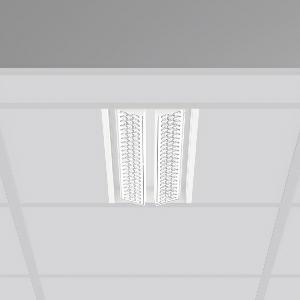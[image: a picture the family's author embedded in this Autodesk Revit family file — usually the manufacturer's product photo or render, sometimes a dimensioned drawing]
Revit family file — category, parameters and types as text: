
# Revit family: tx-move_901736_002_3_d08b
name_source: partatom
category: Lighting Fixtures
units: mm (PartAtom-declared; Revit-internal decimal feet)

## family parameters
Cut with Voids When Loaded = No
Host = Face
Light Source = No
Part Type = Normal
Room Calculation Point = No
Round Connector Dimension = Use Diameter
Shared = No

## types (1)
- MultiLumen 1 (1 x LED Modul 835, 2775 lm, 3500)
    Apparent Load = 35 VA
    CIE Flux Codes = 88 96 99 100 100
    Color Rendering = 80
    Color Temperature = 3500
    Default Elevation = 1800 mm
    Description = Series: TX-MOVE
Einlege/Einbau-Flächenstrahler. Housing: sheet steel, powder-coated. 2xSwivel range: 90°. High-efficiency LED units with optimum light control thanks to clear plastic (PC) lens optics. Spezielle Mikrostrukturen reduzieren Gelbsaum. Symmetrical light distribution. Suitable for laying in grid ceiling module 625. Connected converter included in separate gearbox.Suitable for through-wiring.MultiLumen: Luminous flux adjustable in 3 steps. Accessories: Mounting frame for installation in suspended ceilings. Environmentally friendly and resource-saving due to replaceable and recyclable components. 
Colour: traffic white, matt (RAL 9016)
Length: 622 mm
Width: 190 mm
Height: 39 mm
Cut-out length: 602 mm
Cut-out width: 174 mm
Recess height: 100 mm
Lamp: LED
Socket: without socket
Colour temperature: 3500K
Colour rendering index (CRI): 80
System power: 35 W
Rated luminous flux: 5550 lm
Luminous efficiency: 159 lm/W
System power 2: 47 W
Rated luminous flux 2: 7200 lm
Luminous efficiency 2: 153 lm/W
System power 3: 68 W
Rated luminous flux 3: 9900 lm
Luminous efficiency 3: 146 lm/W
Control gear: Regulated power supply
Protection class: I
Type of protection: IP 20
    Height = 0 mm  [stored 0 ft]
    Lamp = 1 x LED Modul 835
    Lamp Light Flux = 2775 lm
    Lamp count = 1
    Length = 622 mm
    Lifetime = 50000 h
    Luminous efficacy = 159 lm/W
    Manufacturer = RZB
    ModVariant = No
    Model = 901736.002.3
    Mounting Place = Ceiling, Wall
    Mounting Type = Recessed
    Number of Poles = 1
    OnlyDefault = Yes
    Power Factor = 1
    Product Name = TX-MOVE
    Product group = Recessed projectors
    ProductGroupID = 401
    Protection Class = Protection class I
    Protection Degree = IP 20
    RLX_Detail_Level = 1
    RLX_Emergency_Light_Flux = 0 lm
    RLX_Emergency_Type = 0
    RLX_Emergency_Type_DB = No
    RlxData = <blob elided: 34185 chars, md5=436d092a>
    Socket = socket
    Standby Power = 0 W
    System Light Flux = 5550 lm
    System Power = 35 W
    Type Comments = MultiLumen 1
    Type Image = 901737.002.jpg
    URL = http://relux.com
    VarID = multilumen_1
    Voltage = 230 V
    Voltage Range = 220-240 V
    Weight = 0.00 kg
    Width = 190 mm  [stored 0.62336 ft]

note: [stored X ft] marks values corroborated as IEEE doubles in the binary element streams (Revit-internal decimal feet)

## geometry (parser evidence)
native form markers: Blend x4, Sweep x14
no freeform markers — native parametric forms only
